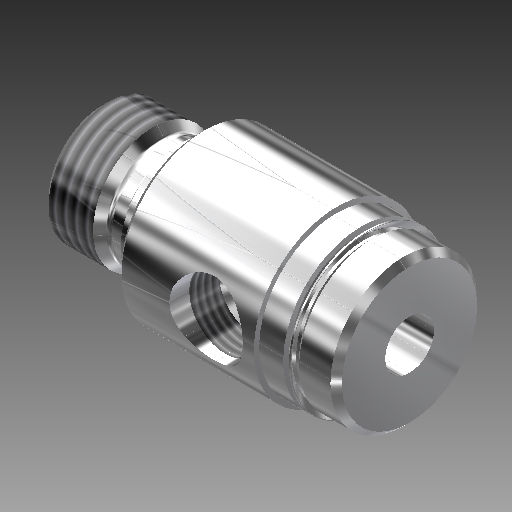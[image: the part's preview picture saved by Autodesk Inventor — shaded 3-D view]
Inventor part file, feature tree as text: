
AUTODESK INVENTOR PART (.ipt)
format: ipt  version: 2017 (Build 210142000, 142)  size: 367,104 bytes
history: native  units: in
note: dims shown in document units (in); Inventor stores cm internally (conversion verified against a paired STEP export)
features: other x119, sketch x6, revolve x5, thread x2, hole x1
ambient origin geometry x8: Origin, YZ Plane, XZ Plane, XY Plane, X Axis, Y Axis, Z Axis, Center Point
bodies: Solid1 (feature_tree)
feature tree (133):
  revolve  "Revolution1"  [1 undecoded]
  thread  "Thread1"  [1 undecoded]
  revolve  "Revolution2"  Angle=360.0deg
  hole  "Hole1"  [1 undecoded]
  revolve  "Revolution3"  [1 undecoded]
  revolve  "Revolution4"  [1 undecoded]
  thread  "Thread2"  [1 undecoded]
  revolve  "Revolution5"  [1 undecoded]
  other  "dp1_XY"
  other  "dp1_YZ"
  other  "dp1_ZX"
  other  "dp1_X"
  other  "dp1_Y"
  other  "dp1_Z"
  other  "dp1_Center"
  other  "dp2_XY"
  other  "dp2_YZ"
  other  "dp2_ZX"
  other  "dp2_X"
  other  "dp2_Y"
  other  "dp2_Z"
  other  "dp2_Center"
  other  "hh_XY"
  other  "hh_YZ"
  other  "hh_ZX"
  other  "hh_X"
  other  "hh_Y"
  other  "hh_Z"
  other  "hh_Center"
  other  "port_XY"
  other  "port_YZ"
  other  "port_ZX"
  other  "port_X"
  other  "port_Y"
  other  "port_Z"
  other  "port_Center"
  other  "rod_guide_XY"
  other  "rod_guide_YZ"
  other  "rod_guide_ZX"
  other  "rod_guide_X"
  other  "rod_guide_Y"
  other  "rod_guide_Z"
  other  "rod_guide_Center"
  other  "s1_XY"
  other  "s1_YZ"
  other  "s1_ZX"
  other  "s1_X"
  other  "s1_Y"
  other  "s1_Z"
  other  "s1_Center"
  other  "s2_XY"
  other  "s2_YZ"
  other  "s2_ZX"
  other  "s2_X"
  other  "s2_Y"
  other  "s2_Z"
  other  "s2_Center"
  other  "t1_XY"
  other  "t1_YZ"
  other  "t1_ZX"
  other  "t1_X"
  other  "t1_Y"
  other  "t1_Z"
  other  "t1_Center"
  other  "t111_XY"
  other  "t111_YZ"
  other  "t111_ZX"
  other  "t111_X"
  other  "t111_Y"
  other  "t111_Z"
  other  "t111_Center"
  other  "to_foot_bracket_XY"
  other  "to_foot_bracket_YZ"
  other  "to_foot_bracket_ZX"
  other  "to_foot_bracket_X"
  other  "to_foot_bracket_Y"
  other  "to_foot_bracket_Z"
  other  "to_foot_bracket_Center"
  other  "to_nut_XY"
  other  "to_nut_YZ"
  other  "to_nut_ZX"
  other  "to_nut_X"
  other  "to_nut_Y"
  other  "to_nut_Z"
  other  "to_nut_Center"
  other  "to_rod_XY"
  other  "to_rod_YZ"
  other  "to_rod_ZX"
  other  "to_rod_X"
  other  "to_rod_Y"
  other  "to_rod_Z"
  other  "to_rod_Center"
  other  "to_screw_XY"
  other  "to_screw_YZ"
  other  "to_screw_ZX"
  other  "to_screw_X"
  other  "to_screw_Y"
  other  "to_screw_Z"
  other  "to_screw_Center"
  other  "to_trunnion_brackets_XY"
  other  "to_trunnion_brackets_YZ"
  other  "to_trunnion_brackets_ZX"
  other  "to_trunnion_brackets_X"
  other  "to_trunnion_brackets_Y"
  other  "to_trunnion_brackets_Z"
  other  "to_trunnion_brackets_Center"
  other  "to_trunnion_brackets1_XY"
  other  "to_trunnion_brackets1_YZ"
  other  "to_trunnion_brackets1_ZX"
  other  "to_trunnion_brackets1_X"
  other  "to_trunnion_brackets1_Y"
  other  "to_trunnion_brackets1_Z"
  other  "to_trunnion_brackets1_Center"
  other  "to_trunnion_brackets2_XY"
  other  "to_trunnion_brackets2_YZ"
  other  "to_trunnion_brackets2_ZX"
  other  "to_trunnion_brackets2_X"
  other  "to_trunnion_brackets2_Y"
  other  "to_trunnion_brackets2_Z"
  other  "to_trunnion_brackets2_Center"
  other  "to_tube_XY"
  other  "to_tube_YZ"
  other  "to_tube_ZX"
  other  "to_tube_X"
  other  "to_tube_Y"
  other  "to_tube_Z"
  other  "to_tube_Center"
  sketch  "Sketch_2"  dims[d0=360.0deg d1=0.23in d2=0.0in d3=360.0deg]
  sketch  "Sketch_3"  dims[d4=0.2535in d5=0.75in d6=0.2735in d7=0.25in d8=90.0deg d9=1.594in d10=0.0in d11=360.0deg]
  sketch  "Sketch3"  dims[d12=360.0deg d13=0.1501in d14=0.0in]
  sketch  "Sketch_10"  dims[d15=360.0deg]
  sketch  "Sketch_40"  dims[d16=0.0in d17=0.0in d18=0.0in d19=0.0in d20=0.0in d21=0.0in]
  sketch  "Sketch_47"
note: 7 required parameter values undecoded (feature->parameter linkage not recoverable at this tier; creation-order binding heuristic only, values carry confidence <= 0.55)